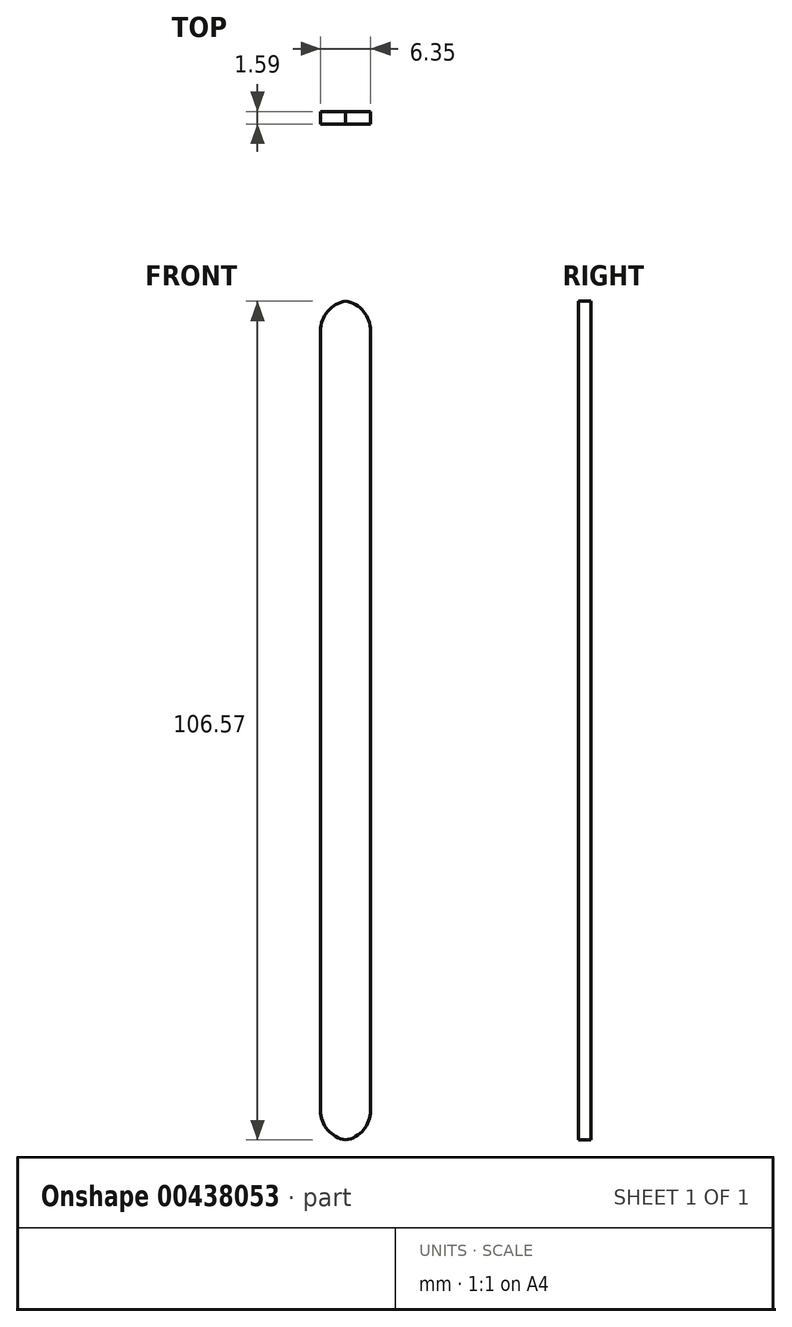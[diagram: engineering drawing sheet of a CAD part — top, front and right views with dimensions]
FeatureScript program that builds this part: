
annotation { "Feature Type Name" : "Feature", "Feature Type Description" : "" }
export const myFeature = defineFeature(function(context is Context, id is Id, definition is map)
    precondition{}
    {
        {
            var Q0;
            Q0=qCreatedBy(makeId("Front.planeOp"),FACE);
            var sketch = newSketch(context, id + "F0", { "sketchPlane" : qUnion([Q0])});
            skLineSegment(sketch, "E0.bottom", {"start": v(-36.1, -65.54) * mm, "end": v(-29.74, -65.54) * mm});
            skLineSegment(sketch, "E0.top", {"start": v(-36.1, 41.14) * mm, "end": v(-29.74, 41.14) * mm});
            skLineSegment(sketch, "E0.left", {"start": v(-36.1, -65.54) * mm, "end": v(-36.1, 41.14) * mm});
            skLineSegment(sketch, "E0.right", {"start": v(-29.74, -65.54) * mm, "end": v(-29.74, 41.14) * mm});
            skSolve(sketch);
        }
        {
            var Q0;
            Q0=makeQuery(id+"F0.imprint","IMPRINT",FACE,{"disambiguationData":[TD([[makeQuery(id+"F0.imprint","IMPRINT",EDGE,{"derivedFrom":sQuery(id+"F0.wireOp",EDGE,"E0.bottom")}),1.0]])]});
            extrude(context, id + "F1", {"entities" : qUnion([Q0]), "depth" : 1.59 * mm, "offsetDistance" : 25.4 * mm});
        }
        {
            var Q0;
            Q0=makeQuery(id+"F1.opExtrude","SWEPT_EDGE",EDGE,{"disambiguationData":[OSD([sQuery(id+"F0.wireOp",EDGE,"E0.top"),sQuery(id+"F0.wireOp",EDGE,"E0.left")])]});
            var Q1;
            Q1=makeQuery(id+"F1.opExtrude","SWEPT_EDGE",EDGE,{"disambiguationData":[OSD([sQuery(id+"F0.wireOp",EDGE,"E0.top"),sQuery(id+"F0.wireOp",EDGE,"E0.right")])]});
            fillet(context, id + "F2", {"entities" : qUnion([Q0, Q1]), "radius" : 3.8 * mm, "tangentPropagation" : true, "allowEdgeOverflow" : false});
        }
        {
            var Q0;
            Q0=makeQuery(id+"F1.opExtrude","SWEPT_EDGE",EDGE,{"disambiguationData":[OSD([sQuery(id+"F0.wireOp",EDGE,"E0.bottom"),sQuery(id+"F0.wireOp",EDGE,"E0.left")])]});
            var Q1;
            Q1=makeQuery(id+"F1.opExtrude","SWEPT_EDGE",EDGE,{"disambiguationData":[OSD([sQuery(id+"F0.wireOp",EDGE,"E0.bottom"),sQuery(id+"F0.wireOp",EDGE,"E0.right")])]});
            fillet(context, id + "F3", {"entities" : qUnion([Q0, Q1]), "radius" : 3.8 * mm, "tangentPropagation" : true, "allowEdgeOverflow" : false});
        }
    });
